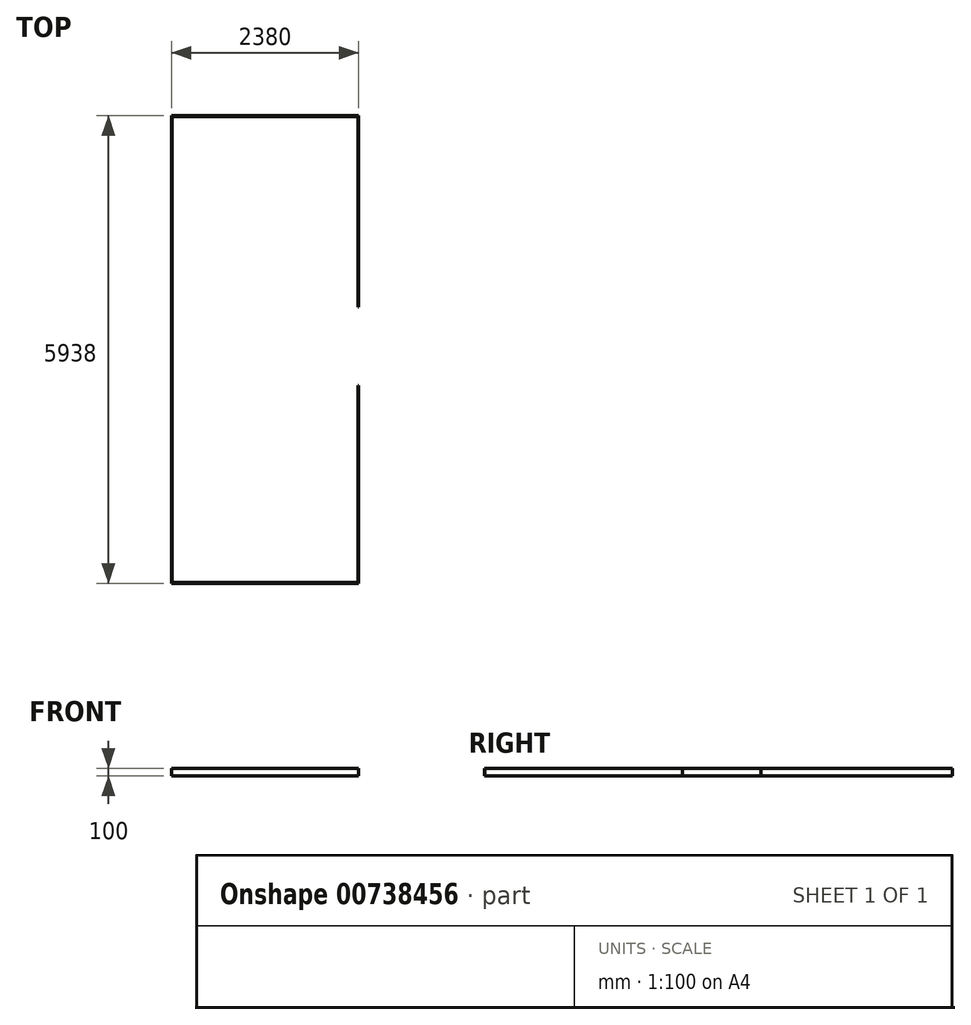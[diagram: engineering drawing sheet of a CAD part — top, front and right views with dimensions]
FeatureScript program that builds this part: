
annotation { "Feature Type Name" : "Feature", "Feature Type Description" : "" }
export const myFeature = defineFeature(function(context is Context, id is Id, definition is map)
    precondition{}
    {
        {
            var Q0;
            Q0=qCreatedBy(makeId("Top.planeOp"),FACE);
            var sketch = newSketch(context, id + "F0", { "sketchPlane" : qUnion([Q0])});
            skLineSegment(sketch, "E0.bottom", {"start": v(0, 0) * mm, "end": v(2380, 0) * mm});
            skLineSegment(sketch, "E0.top", {"start": v(0, 5938) * mm, "end": v(2380, 5938) * mm});
            skLineSegment(sketch, "E0.left", {"start": v(0, 0) * mm, "end": v(0, 5938) * mm});
            skLineSegment(sketch, "E0.right", {"start": v(2380, 0) * mm, "end": v(2380, 5938) * mm});
            skLineSegment(sketch, "E1.bottom", {"start": v(10, 10) * mm, "end": v(2370, 10) * mm});
            skLineSegment(sketch, "E1.top", {"start": v(10, 5928) * mm, "end": v(2370, 5928) * mm});
            skLineSegment(sketch, "E1.left", {"start": v(10, 10) * mm, "end": v(10, 5928) * mm});
            skLineSegment(sketch, "E1.right", {"start": v(2370, 10) * mm, "end": v(2370, 5928) * mm});
            skSolve(sketch);
        }
        {
            var Q0;
            Q0 = qSketchRegion(id + "F0", true);
            extrude(context, id + "F1", {"entities" : qUnion([Q0]), "depth" : 100 * mm, "offsetDistance" : 25 * mm});
        }
        {
            var Q0;
            Q0=makeQuery(id+"F1.opExtrude","SWEPT_FACE",FACE,{"disambiguationData":[OSD([sQuery(id+"F0.wireOp",EDGE,"E0.right")])]});
            var sketch = newSketch(context, id + "F2", { "sketchPlane" : qUnion([Q0])});
            skLineSegment(sketch, "E2.bottom", {"start": v(2510, 100) * mm, "end": v(3510, 100) * mm});
            skLineSegment(sketch, "E2.top", {"start": v(2510, 0) * mm, "end": v(3510, 0) * mm});
            skLineSegment(sketch, "E2.left", {"start": v(2510, 100) * mm, "end": v(2510, 0) * mm});
            skLineSegment(sketch, "E2.right", {"start": v(3510, 100) * mm, "end": v(3510, 0) * mm});
            skSolve(sketch);
        }
        {
            var Q0;
            Q0=makeQuery(id+"F2.imprint","IMPRINT",FACE,{"disambiguationData":[TD([[makeQuery(id+"F2.imprint","IMPRINT",EDGE,{"derivedFrom":sQuery(id+"F2.wireOp",EDGE,"E2.bottom")}),-1.0]])]});
            extrude(context, id + "F3", {"entities" : qUnion([Q0]), "operationType" : NewBodyOperationType.REMOVE, "oppositeDirection" : true, "depth" : 25 * mm, "offsetDistance" : 25 * mm});
        }
    });
